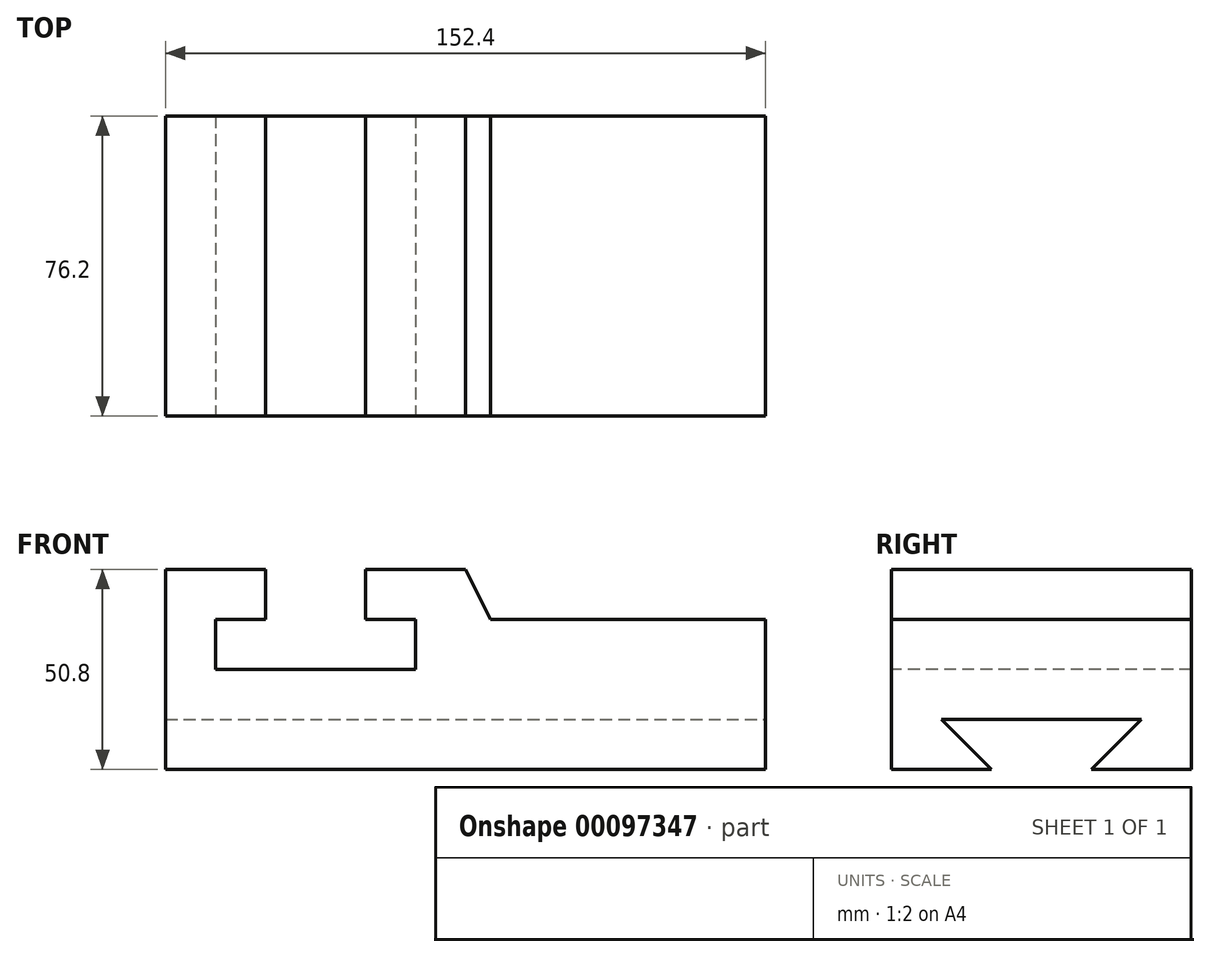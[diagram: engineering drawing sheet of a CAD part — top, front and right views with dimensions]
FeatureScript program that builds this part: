
annotation { "Feature Type Name" : "Feature", "Feature Type Description" : "" }
export const myFeature = defineFeature(function(context is Context, id is Id, definition is map)
    precondition{}
    {
        {
            var Q0;
            Q0=qCreatedBy(makeId("Front.planeOp"),FACE);
            var sketch = newSketch(context, id + "F0", { "sketchPlane" : qUnion([Q0])});
            skLineSegment(sketch, "E0", {"start": v(0, 0) * mm, "end": v(76.2, 0) * mm});
            skLineSegment(sketch, "E1", {"start": v(76.2, 0) * mm, "end": v(76.2, 38.1) * mm});
            skLineSegment(sketch, "E2", {"start": v(76.2, 38.1) * mm, "end": v(6.35, 38.1) * mm});
            skLineSegment(sketch, "E3", {"start": v(6.35, 38.1) * mm, "end": v(0, 50.8) * mm});
            skLineSegment(sketch, "E4", {"start": v(0, 50.8) * mm, "end": v(-76.2, 50.8) * mm});
            skLineSegment(sketch, "E5", {"start": v(-76.2, 50.8) * mm, "end": v(-76.2, 0) * mm});
            skLineSegment(sketch, "E6", {"start": v(-76.2, 0) * mm, "end": v(0, 0) * mm});
            skSolve(sketch);
        }
        {
            var Q0;
            Q0=makeQuery(id+"F0.imprint","IMPRINT",FACE,{"disambiguationData":[TD([[makeQuery(id+"F0.imprint","IMPRINT",EDGE,{"derivedFrom":sQuery(id+"F0.wireOp",EDGE,"E0")}),1.0]])]});
            extrude(context, id + "F1", {"entities" : qUnion([Q0]), "depth" : 76.2 * mm, "symmetric" : true});
        }
        {
            var Q0;
            Q0=makeQuery(id+"F1.opExtrude","CAP_FACE",FACE,{"disambiguationData":[OSD([sQuery(id+"F0.wireOp",EDGE,"E0"),sQuery(id+"F0.wireOp",EDGE,"E1"),sQuery(id+"F0.wireOp",EDGE,"E2"),sQuery(id+"F0.wireOp",EDGE,"E3"),sQuery(id+"F0.wireOp",EDGE,"E4"),sQuery(id+"F0.wireOp",EDGE,"E5"),sQuery(id+"F0.wireOp",EDGE,"E6")])],"isStart":false});
            var sketch = newSketch(context, id + "F2", { "sketchPlane" : qUnion([Q0])});
            skLineSegment(sketch, "E7", {"start": v(-50.8, 50.8) * mm, "end": v(-50.8, 38.1) * mm});
            skLineSegment(sketch, "E8", {"start": v(-50.8, 38.1) * mm, "end": v(-63.5, 38.1) * mm});
            skLineSegment(sketch, "E9", {"start": v(-63.5, 38.1) * mm, "end": v(-63.5, 25.4) * mm});
            skLineSegment(sketch, "E10", {"start": v(-63.5, 25.4) * mm, "end": v(-12.7, 25.4) * mm});
            skLineSegment(sketch, "E11", {"start": v(-12.7, 25.4) * mm, "end": v(-12.7, 38.1) * mm});
            skLineSegment(sketch, "E12", {"start": v(-12.7, 38.1) * mm, "end": v(-25.4, 38.1) * mm});
            skLineSegment(sketch, "E13", {"start": v(-25.4, 38.1) * mm, "end": v(-25.4, 50.8) * mm});
            skLineSegment(sketch, "E14", {"start": v(-25.4, 50.8) * mm, "end": v(-50.8, 50.8) * mm});
            skSolve(sketch);
        }
        {
            var Q0;
            Q0=makeQuery(id+"F2.imprint","IMPRINT",FACE,{"disambiguationData":[TD([[makeQuery(id+"F2.imprint","IMPRINT",EDGE,{"derivedFrom":sQuery(id+"F2.wireOp",EDGE,"E7")}),1.0]])]});
            extrude(context, id + "F3", {"entities" : qUnion([Q0]), "operationType" : NewBodyOperationType.REMOVE, "endBound" : BoundingType.THROUGH_ALL, "oppositeDirection" : true, "depth" : 25.4 * mm});
        }
        {
            var Q0;
            Q0=makeQuery(id+"F1.opExtrude","SWEPT_FACE",FACE,{"disambiguationData":[OSD([sQuery(id+"F0.wireOp",EDGE,"E1")])]});
            var sketch = newSketch(context, id + "F4", { "sketchPlane" : qUnion([Q0])});
            skLineSegment(sketch, "E15", {"start": v(-12.7, 0) * mm, "end": v(-25.4, 12.7) * mm});
            skLineSegment(sketch, "E16", {"start": v(-25.4, 12.7) * mm, "end": v(25.4, 12.7) * mm});
            skLineSegment(sketch, "E17", {"start": v(25.4, 12.7) * mm, "end": v(12.7, 0) * mm});
            skLineSegment(sketch, "E18", {"start": v(12.7, 0) * mm, "end": v(-12.7, 0) * mm});
            skSolve(sketch);
        }
        {
            var Q0;
            Q0=makeQuery(id+"F4.imprint","IMPRINT",FACE,{"disambiguationData":[TD([[makeQuery(id+"F4.imprint","IMPRINT",EDGE,{"derivedFrom":sQuery(id+"F4.wireOp",EDGE,"E15")}),-1.0]])]});
            extrude(context, id + "F5", {"entities" : qUnion([Q0]), "operationType" : NewBodyOperationType.REMOVE, "endBound" : BoundingType.THROUGH_ALL, "oppositeDirection" : true, "depth" : 25.4 * mm});
        }
    });
